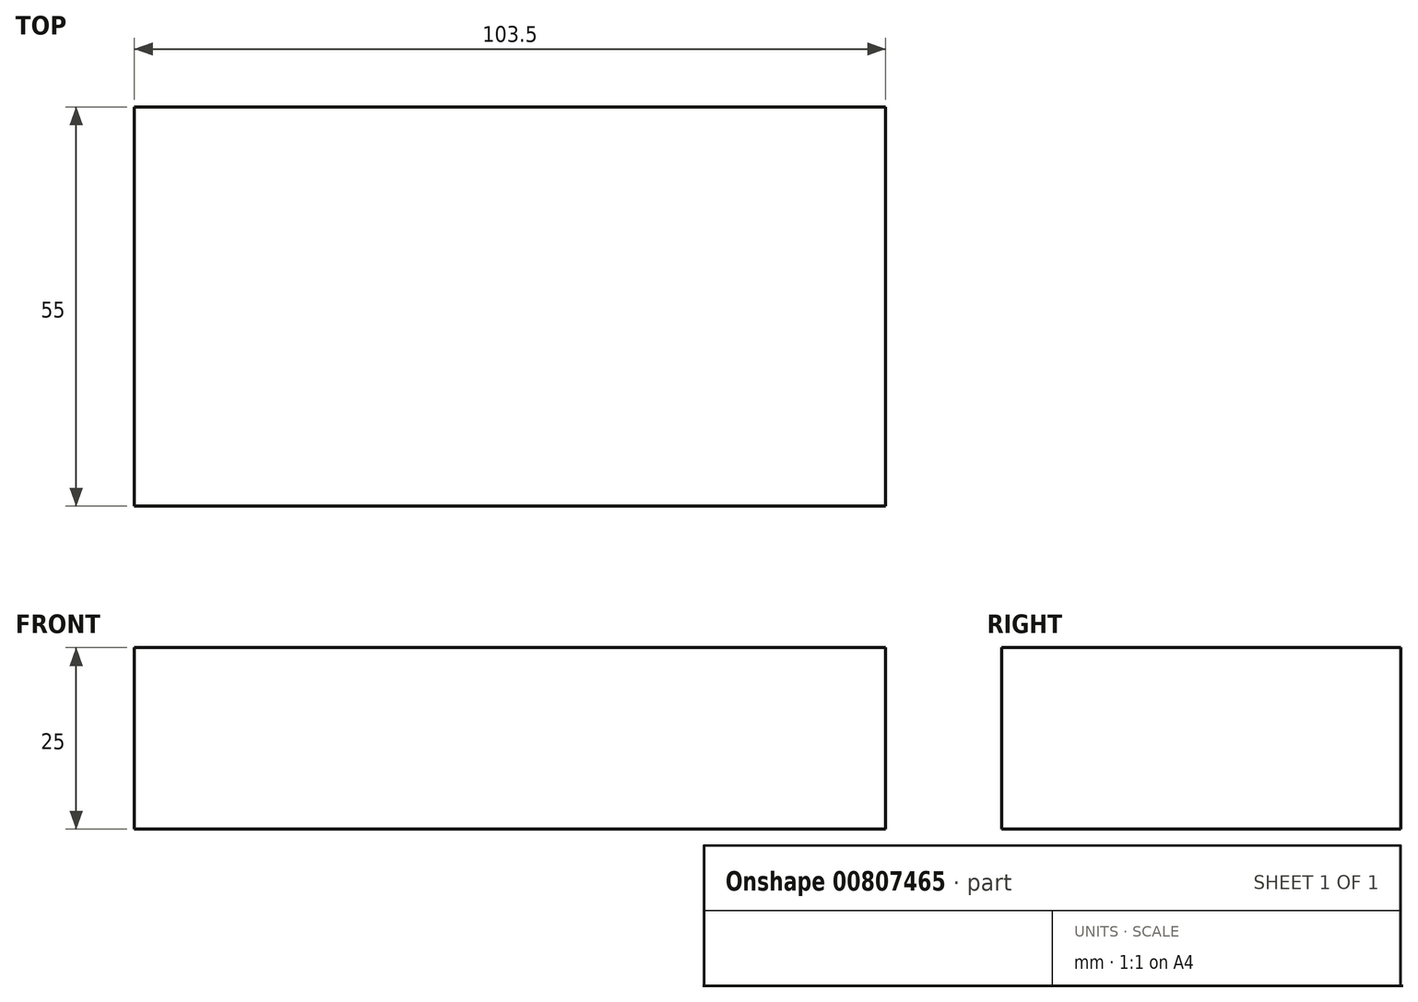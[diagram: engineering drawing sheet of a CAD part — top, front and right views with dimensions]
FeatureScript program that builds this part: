
annotation { "Feature Type Name" : "Feature", "Feature Type Description" : "" }
export const myFeature = defineFeature(function(context is Context, id is Id, definition is map)
    precondition{}
    {
        {
            var Q0;
            Q0=qCreatedBy(makeId("Front.planeOp"),FACE);
            var sketch = newSketch(context, id + "F0", { "sketchPlane" : qUnion([Q0])});
            skLineSegment(sketch, "E0.bottom", {"start": v(-51.75, 12.5) * mm, "end": v(51.75, 12.5) * mm});
            skLineSegment(sketch, "E0.top", {"start": v(-51.75, -12.5) * mm, "end": v(51.75, -12.5) * mm});
            skLineSegment(sketch, "E0.left", {"start": v(-51.75, 12.5) * mm, "end": v(-51.75, -12.5) * mm});
            skLineSegment(sketch, "E0.right", {"start": v(51.75, 12.5) * mm, "end": v(51.75, -12.5) * mm});
            skPoint(sketch, "E0.middle", {"position": v(0, 0) * mm});
            skSolve(sketch);
        }
        {
            var Q0;
            Q0=makeQuery(id+"F0.imprint","IMPRINT",FACE,{"disambiguationData":[TD([[makeQuery(id+"F0.imprint","IMPRINT",EDGE,{"derivedFrom":sQuery(id+"F0.wireOp",EDGE,"E0.bottom")}),-1.0]])]});
            extrude(context, id + "F1", {"entities" : qUnion([Q0]), "depth" : 55 * mm, "offsetDistance" : 25.4 * mm});
        }
    });
